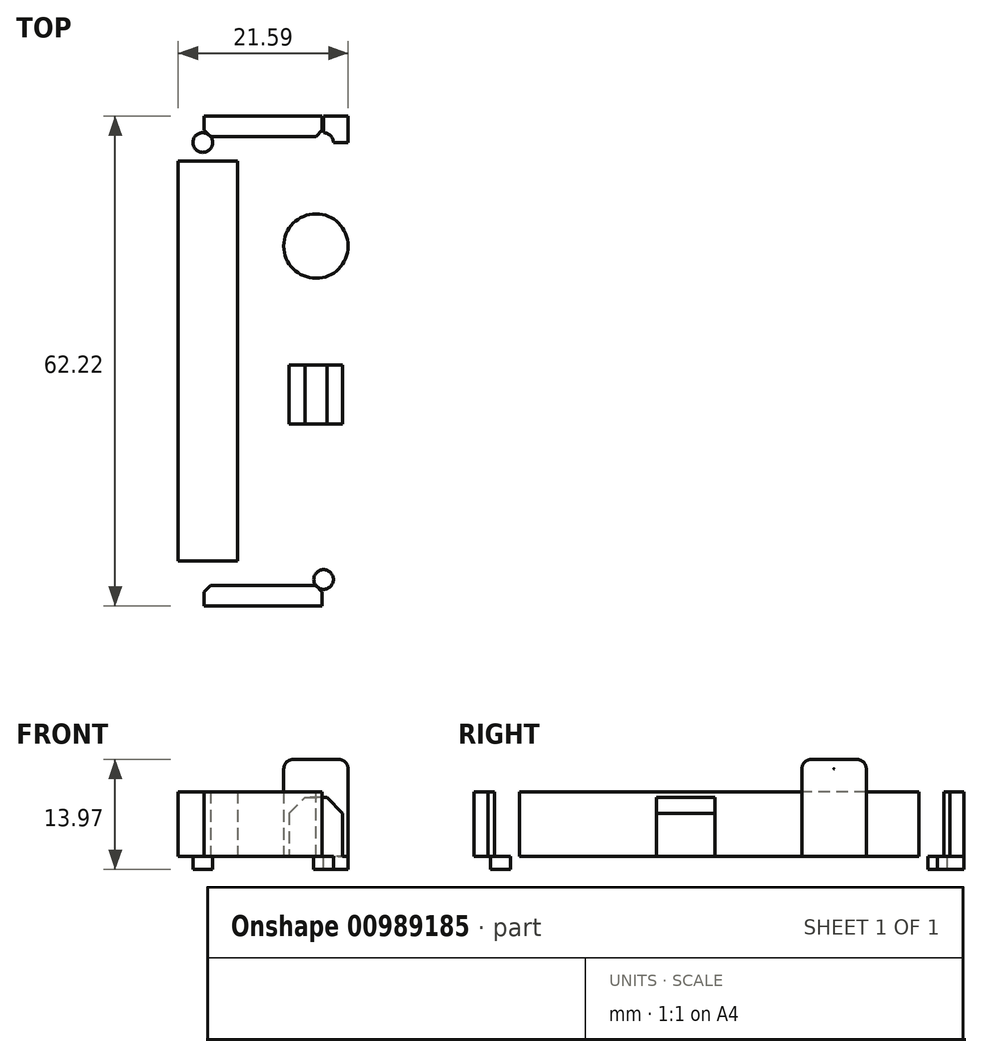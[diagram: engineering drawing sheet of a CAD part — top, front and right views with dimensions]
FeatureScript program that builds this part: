
annotation { "Feature Type Name" : "Feature", "Feature Type Description" : "" }
export const myFeature = defineFeature(function(context is Context, id is Id, definition is map)
    precondition{}
    {
        {
            var Q0;
            Q0=qCreatedBy(makeId("Top.planeOp"),FACE);
            var sketch = newSketch(context, id + "F0", { "sketchPlane" : qUnion([Q0])});
            skLineSegment(sketch, "E0.bottom", {"start": v(-10.8, -31.1) * mm, "end": v(10.8, -31.1) * mm});
            skLineSegment(sketch, "E0.top", {"start": v(-10.8, 31.1) * mm, "end": v(10.8, 31.1) * mm});
            skLineSegment(sketch, "E0.left", {"start": v(-10.8, -31.1) * mm, "end": v(-10.8, 31.1) * mm});
            skLineSegment(sketch, "E0.right", {"start": v(10.8, -31.1) * mm, "end": v(10.8, 31.1) * mm});
            skPoint(sketch, "E0.middle", {"position": v(0, 0) * mm});
            skSolve(sketch);
        }
        {
            var Q0;
            Q0=qSketchRegion(id+"F0",true);
            extrude(context, id + "F1", {"entities" : qUnion([Q0]), "depth" : 1.63 * mm, "offsetDistance" : 25 * mm});
        }
        {
            var Q0;
            Q0=makeQuery(id+"F1.opExtrude","CAP_FACE",FACE,{"disambiguationData":[OSD([sQuery(id+"F0.wireOp",EDGE,"E0.bottom"),sQuery(id+"F0.wireOp",EDGE,"E0.top"),sQuery(id+"F0.wireOp",EDGE,"E0.left"),sQuery(id+"F0.wireOp",EDGE,"E0.right")])],"isStart":false});
            var sketch = newSketch(context, id + "F2", { "sketchPlane" : qUnion([Q0])});
            skCircle(sketch, "E1", {"center": v(7.67, 27.75) * mm, "radius": 1.25 * mm});
            skLineSegment(sketch, "E2.bottom", {"start": v(10.8, 31.1) * mm, "end": v(7.67, 31.1) * mm});
            skLineSegment(sketch, "E2.top", {"start": v(10.8, 27.75) * mm, "end": v(7.67, 27.75) * mm});
            skLineSegment(sketch, "E2.left", {"start": v(10.8, 31.1) * mm, "end": v(10.8, 27.75) * mm});
            skLineSegment(sketch, "E2.right", {"start": v(7.67, 31.1) * mm, "end": v(7.67, 27.75) * mm});
            skCircle(sketch, "E3.MirrorC", {"center": v(-7.67, 27.75) * mm, "radius": 1.25 * mm});
            skCircle(sketch, "E4.MirrorC", {"center": v(-7.67, -27.75) * mm, "radius": 1.25 * mm});
            skCircle(sketch, "E5.MirrorC", {"center": v(7.67, -27.75) * mm, "radius": 1.25 * mm});
            skSolve(sketch);
        }
        {
            var Q0;
            Q0=makeQuery(id+"F1.opExtrude","CAP_FACE",FACE,{"disambiguationData":[OSD([sQuery(id+"F0.wireOp",EDGE,"E0.bottom"),sQuery(id+"F0.wireOp",EDGE,"E0.top"),sQuery(id+"F0.wireOp",EDGE,"E0.left"),sQuery(id+"F0.wireOp",EDGE,"E0.right")])],"isStart":false});
            var sketch = newSketch(context, id + "F3", { "sketchPlane" : qUnion([Q0])});
            skLineSegment(sketch, "E6", {"start": v(6.7, 31.1) * mm, "end": v(6.7, 14.6) * mm});
            skCircle(sketch, "E7", {"center": v(6.7, 14.6) * mm, "radius": 4.1 * mm});
            skLineSegment(sketch, "E8", {"start": v(6.7, 10.52) * mm, "end": v(6.7, -0.52) * mm});
            skPoint(sketch, "E9.middle", {"position": v(6.7, -7.07) * mm});
            skPoint(sketch, "E10.middle", {"position": v(20.4, -12.22) * mm});
            skLineSegment(sketch, "E11", {"start": v(6.7, -0.52) * mm, "end": v(3.32, -0.52) * mm});
            skLineSegment(sketch, "E12.MirrorCS", {"start": v(6.7, -0.52) * mm, "end": v(10.1, -0.52) * mm});
            skLineSegment(sketch, "E13", {"start": v(3.32, -0.52) * mm, "end": v(3.32, -7.97) * mm});
            skLineSegment(sketch, "E14", {"start": v(10.1, -0.52) * mm, "end": v(10.1, -7.97) * mm});
            skLineSegment(sketch, "E15", {"start": v(10.1, -7.97) * mm, "end": v(3.32, -7.97) * mm});
            skSolve(sketch);
        }
        {
            var Q0;
            {var subQ0=sQuery(id+"F3.wireOp",EDGE,"E7");var subQ5=makeQuery(id+"F3.imprint","IMPRINT",VERTEX,{"derivedFrom":subQ0});Q0=makeQuery(id+"F3.imprint","IMPRINT",FACE,{"disambiguationData":[TD([[makeQuery(id+"F3.imprint","IMPRINT",EDGE,{"disambiguationData":[TD([[subQ5,1.0]])],"derivedFrom":subQ0}),1.0]])]});}
            extrude(context, id + "F4", {"entities" : qUnion([Q0]), "depth" : 12.34 * mm, "offsetDistance" : 25 * mm});
        }
        {
            var Q0;
            Q0=makeQuery(id+"F3.imprint","IMPRINT",FACE,{"disambiguationData":[TD([[makeQuery(id+"F3.imprint","IMPRINT",EDGE,{"derivedFrom":sQuery(id+"F3.wireOp",EDGE,"E11")}),1.0]])]});
            extrude(context, id + "F5", {"entities" : qUnion([Q0]), "depth" : 7.5 * mm, "offsetDistance" : 25 * mm});
        }
        {
            var Q0;
            {var subQ0=sQuery(id+"F2.wireOp",EDGE,"E2.top");var subQ1=sQuery(id+"F2.wireOp",EDGE,"E1");var subQ2=makeQuery(id+"F2.imprint","INTERSECT",VERTEX,{"derivedFrom":[subQ1,subQ0]});Q0=makeQuery(id+"F2.imprint","IMPRINT",FACE,{"disambiguationData":[TD([[makeQuery(id+"F2.imprint","IMPRINT",EDGE,{"disambiguationData":[TD([[subQ2,1.0]])],"derivedFrom":subQ1}),1.0]])]});}
            var Q1;
            {var subQ0=sQuery(id+"F2.wireOp",EDGE,"E2.top");var subQ1=sQuery(id+"F2.wireOp",EDGE,"E1");var subQ2=makeQuery(id+"F2.imprint","INTERSECT",VERTEX,{"derivedFrom":[subQ1,subQ0]});Q1=makeQuery(id+"F2.imprint","IMPRINT",FACE,{"disambiguationData":[TD([[makeQuery(id+"F2.imprint","IMPRINT",EDGE,{"disambiguationData":[TD([[subQ2,-1.0]])],"derivedFrom":subQ1}),1.0]])]});}
            var Q2;
            Q2=makeQuery(id+"F2.imprint","IMPRINT",FACE,{"disambiguationData":[TD([[makeQuery(id+"F2.imprint","IMPRINT",EDGE,{"derivedFrom":sQuery(id+"F2.wireOp",EDGE,"E3.MirrorC")}),-1.0]])]});
            var Q3;
            Q3=makeQuery(id+"F2.imprint","IMPRINT",FACE,{"disambiguationData":[TD([[makeQuery(id+"F2.imprint","IMPRINT",EDGE,{"derivedFrom":sQuery(id+"F2.wireOp",EDGE,"E4.MirrorC")}),1.0]])]});
            var Q4;
            Q4=makeQuery(id+"F2.imprint","IMPRINT",FACE,{"disambiguationData":[TD([[makeQuery(id+"F2.imprint","IMPRINT",EDGE,{"derivedFrom":sQuery(id+"F2.wireOp",EDGE,"E5.MirrorC")}),-1.0]])]});
            extrude(context, id + "F6", {"entities" : qUnion([Q0, Q1, Q2, Q3, Q4]), "operationType" : NewBodyOperationType.REMOVE, "oppositeDirection" : true, "depth" : 25 * mm, "offsetDistance" : 25 * mm});
        }
        {
            var Q0;
            Q0=makeQuery(id+"F5.opExtrude","CAP_EDGE",EDGE,{"disambiguationData":[OSD([sQuery(id+"F3.wireOp",EDGE,"E13")])],"isStart":false});
            var Q1;
            Q1=makeQuery(id+"F5.opExtrude","CAP_EDGE",EDGE,{"disambiguationData":[OSD([sQuery(id+"F3.wireOp",EDGE,"E14")])],"isStart":false});
            chamfer(context, id + "F7", {"entities" : qUnion([Q0, Q1]), "width" : 2 * mm, "tangentPropagation" : true});
        }
        {
            var Q0;
            {var subQ0=sQuery(id+"F3.wireOp",EDGE,"E7");var subQ1=makeQuery(id+"F3.imprint","IMPRINT",VERTEX,{"derivedFrom":subQ0});var subQ3=makeQuery(id+"F3.imprint","INTERSECT",VERTEX,{"derivedFrom":[sQuery(id+"F3.wireOp",EDGE,"E6"),subQ0]});Q0=makeQuery(id+"F4.opExtrude","CAP_EDGE",EDGE,{"disambiguationData":[OSD([subQ0]),TDD([makeQuery(id+"F3.imprint","IMPRINT",EDGE,{"disambiguationData":[TD([[subQ3,1.0]])],"derivedFrom":subQ0}),makeQuery(id+"F3.imprint","IMPRINT",EDGE,{"disambiguationData":[TD([[subQ1,1.0]])],"derivedFrom":subQ0}),makeQuery(id+"F3.imprint","IMPRINT",EDGE,{"disambiguationData":[TD([[subQ1,-1.0]])],"derivedFrom":subQ0})])],"isStart":false});}
            fillet(context, id + "F8", {"entities" : qUnion([Q0]), "radius" : 1.2 * mm, "tangentPropagation" : true, "allowEdgeOverflow" : false});
        }
        {
            var Q0;
            Q0=makeQuery(id+"F1.opExtrude","CAP_FACE",FACE,{"disambiguationData":[OSD([sQuery(id+"F0.wireOp",EDGE,"E0.bottom"),sQuery(id+"F0.wireOp",EDGE,"E0.top"),sQuery(id+"F0.wireOp",EDGE,"E0.left"),sQuery(id+"F0.wireOp",EDGE,"E0.right")])],"isStart":false});
            var sketch = newSketch(context, id + "F9", { "sketchPlane" : qUnion([Q0])});
            skPoint(sketch, "E16.middle", {"position": v(-9.76, 0) * mm});
            skLineSegment(sketch, "E17", {"start": v(-10.8, 0) * mm, "end": v(-10.8, 25.38) * mm});
            skLineSegment(sketch, "E18.MirrorCS", {"start": v(-10.8, 0) * mm, "end": v(-10.8, -25.38) * mm});
            skLineSegment(sketch, "E19", {"start": v(-10.8, 25.38) * mm, "end": v(-3.29, 25.38) * mm});
            skLineSegment(sketch, "E20.MirrorCS", {"start": v(-10.8, -25.38) * mm, "end": v(-3.29, -25.38) * mm});
            skLineSegment(sketch, "E21", {"start": v(-3.29, 25.38) * mm, "end": v(-3.29, -25.38) * mm});
            skSolve(sketch);
        }
        {
            var Q0;
            Q0=makeQuery(id+"F9.imprint","IMPRINT",FACE,{"disambiguationData":[TD([[makeQuery(id+"F9.imprint","IMPRINT",EDGE,{"derivedFrom":sQuery(id+"F9.wireOp",EDGE,"E17")}),-1.0]])]});
            extrude(context, id + "F10", {"entities" : qUnion([Q0]), "depth" : 8.23 * mm, "offsetDistance" : 25 * mm});
        }
        {
            var Q0;
            Q0=makeQuery(id+"F1.opExtrude","CAP_FACE",FACE,{"disambiguationData":[OSD([sQuery(id+"F0.wireOp",EDGE,"E0.bottom"),sQuery(id+"F0.wireOp",EDGE,"E0.top"),sQuery(id+"F0.wireOp",EDGE,"E0.left"),sQuery(id+"F0.wireOp",EDGE,"E0.right")])],"isStart":false});
            var sketch = newSketch(context, id + "F11", { "sketchPlane" : qUnion([Q0])});
            skLineSegment(sketch, "E22", {"start": v(0, 31.1) * mm, "end": v(-7.49, 31.1) * mm});
            skLineSegment(sketch, "E23", {"start": v(-7.49, 31.1) * mm, "end": v(-7.49, 28.53) * mm});
            skLineSegment(sketch, "E24.MirrorCS", {"start": v(7.49, 31.1) * mm, "end": v(7.49, 28.53) * mm});
            skLineSegment(sketch, "E25.MirrorCS", {"start": v(0, 31.1) * mm, "end": v(7.49, 31.1) * mm});
            skLineSegment(sketch, "E26", {"start": v(-7.49, 28.53) * mm, "end": v(7.49, 28.53) * mm});
            skLineSegment(sketch, "E27.MirrorCS", {"start": v(-7.49, -28.53) * mm, "end": v(7.49, -28.53) * mm});
            skLineSegment(sketch, "E28.MirrorCS", {"start": v(0, -31.1) * mm, "end": v(-7.49, -31.1) * mm});
            skLineSegment(sketch, "E29.MirrorCS", {"start": v(0, -31.1) * mm, "end": v(7.49, -31.1) * mm});
            skLineSegment(sketch, "E30.MirrorCS", {"start": v(7.49, -31.1) * mm, "end": v(7.49, -28.53) * mm});
            skLineSegment(sketch, "E31.MirrorCS", {"start": v(-7.49, -31.1) * mm, "end": v(-7.49, -28.53) * mm});
            skSolve(sketch);
        }
        {
            var Q0;
            {var subQ6=sQuery(id+"F11.wireOp",EDGE,"E22");Q0=makeQuery(id+"F11.imprint","IMPRINT",FACE,{"disambiguationData":[TD([[makeQuery(id+"F11.imprint","IMPRINT",EDGE,{"derivedFrom":subQ6}),-1.0]])]});}
            var Q1;
            {var subQ0=sQuery(id+"F11.wireOp",EDGE,"E26");var subQ1=sQuery(id+"F11.wireOp",EDGE,"E24.MirrorCS");var subQ2=makeQuery(id+"F11.imprint","INTERSECT",VERTEX,{"derivedFrom":[subQ1,subQ0]});Q1=makeQuery(id+"F11.imprint","IMPRINT",FACE,{"disambiguationData":[TD([[makeQuery(id+"F11.imprint","IMPRINT",EDGE,{"disambiguationData":[TD([[subQ2,1.0]])],"derivedFrom":subQ1}),-1.0]])]});}
            var Q2;
            {var subQ0=sQuery(id+"F11.wireOp",EDGE,"E26");var subQ1=sQuery(id+"F11.wireOp",EDGE,"E23");var subQ2=makeQuery(id+"F11.imprint","INTERSECT",VERTEX,{"derivedFrom":[subQ1,subQ0]});Q2=makeQuery(id+"F11.imprint","IMPRINT",FACE,{"disambiguationData":[TD([[makeQuery(id+"F11.imprint","IMPRINT",EDGE,{"disambiguationData":[TD([[subQ2,1.0]])],"derivedFrom":subQ1}),1.0]])]});}
            var Q3;
            {var subQ5=sQuery(id+"F11.wireOp",EDGE,"E28.MirrorCS");Q3=makeQuery(id+"F11.imprint","IMPRINT",FACE,{"disambiguationData":[TD([[makeQuery(id+"F11.imprint","IMPRINT",EDGE,{"derivedFrom":subQ5}),1.0]])]});}
            var Q4;
            {var subQ0=sQuery(id+"F11.wireOp",EDGE,"E30.MirrorCS");var subQ1=sQuery(id+"F11.wireOp",EDGE,"E27.MirrorCS");var subQ2=makeQuery(id+"F11.imprint","INTERSECT",VERTEX,{"derivedFrom":[subQ1,subQ0]});Q4=makeQuery(id+"F11.imprint","IMPRINT",FACE,{"disambiguationData":[TD([[makeQuery(id+"F11.imprint","IMPRINT",EDGE,{"disambiguationData":[TD([[subQ2,1.0]])],"derivedFrom":subQ1}),-1.0]])]});}
            var Q5;
            {var subQ0=sQuery(id+"F11.wireOp",EDGE,"E31.MirrorCS");var subQ1=sQuery(id+"F11.wireOp",EDGE,"E27.MirrorCS");var subQ2=makeQuery(id+"F11.imprint","INTERSECT",VERTEX,{"derivedFrom":[subQ1,subQ0]});Q5=makeQuery(id+"F11.imprint","IMPRINT",FACE,{"disambiguationData":[TD([[makeQuery(id+"F11.imprint","IMPRINT",EDGE,{"disambiguationData":[TD([[subQ2,-1.0]])],"derivedFrom":subQ1}),-1.0]])]});}
            extrude(context, id + "F12", {"entities" : qUnion([Q0, Q1, Q2, Q3, Q4, Q5]), "depth" : 8.23 * mm, "offsetDistance" : 25 * mm});
        }
        {
            var Q0;
            Q0=makeQuery(id+"F12.opExtrude","SWEPT_EDGE",EDGE,{"disambiguationData":[OSD([sQuery(id+"F11.wireOp",EDGE,"E23"),sQuery(id+"F11.wireOp",EDGE,"E26")])]});
            var Q1;
            Q1=makeQuery(id+"F12.opExtrude","SWEPT_EDGE",EDGE,{"disambiguationData":[OSD([sQuery(id+"F11.wireOp",EDGE,"E24.MirrorCS"),sQuery(id+"F11.wireOp",EDGE,"E26")])]});
            var Q2;
            Q2=makeQuery(id+"F12.opExtrude","SWEPT_EDGE",EDGE,{"disambiguationData":[OSD([sQuery(id+"F11.wireOp",EDGE,"E27.MirrorCS"),sQuery(id+"F11.wireOp",EDGE,"E31.MirrorCS")])]});
            var Q3;
            Q3=makeQuery(id+"F12.opExtrude","SWEPT_EDGE",EDGE,{"disambiguationData":[OSD([sQuery(id+"F11.wireOp",EDGE,"E27.MirrorCS"),sQuery(id+"F11.wireOp",EDGE,"E30.MirrorCS")])]});
            chamfer(context, id + "F13", {"entities" : qUnion([Q0, Q1, Q2, Q3]), "width" : 0.8 * mm, "tangentPropagation" : true});
        }
    });
